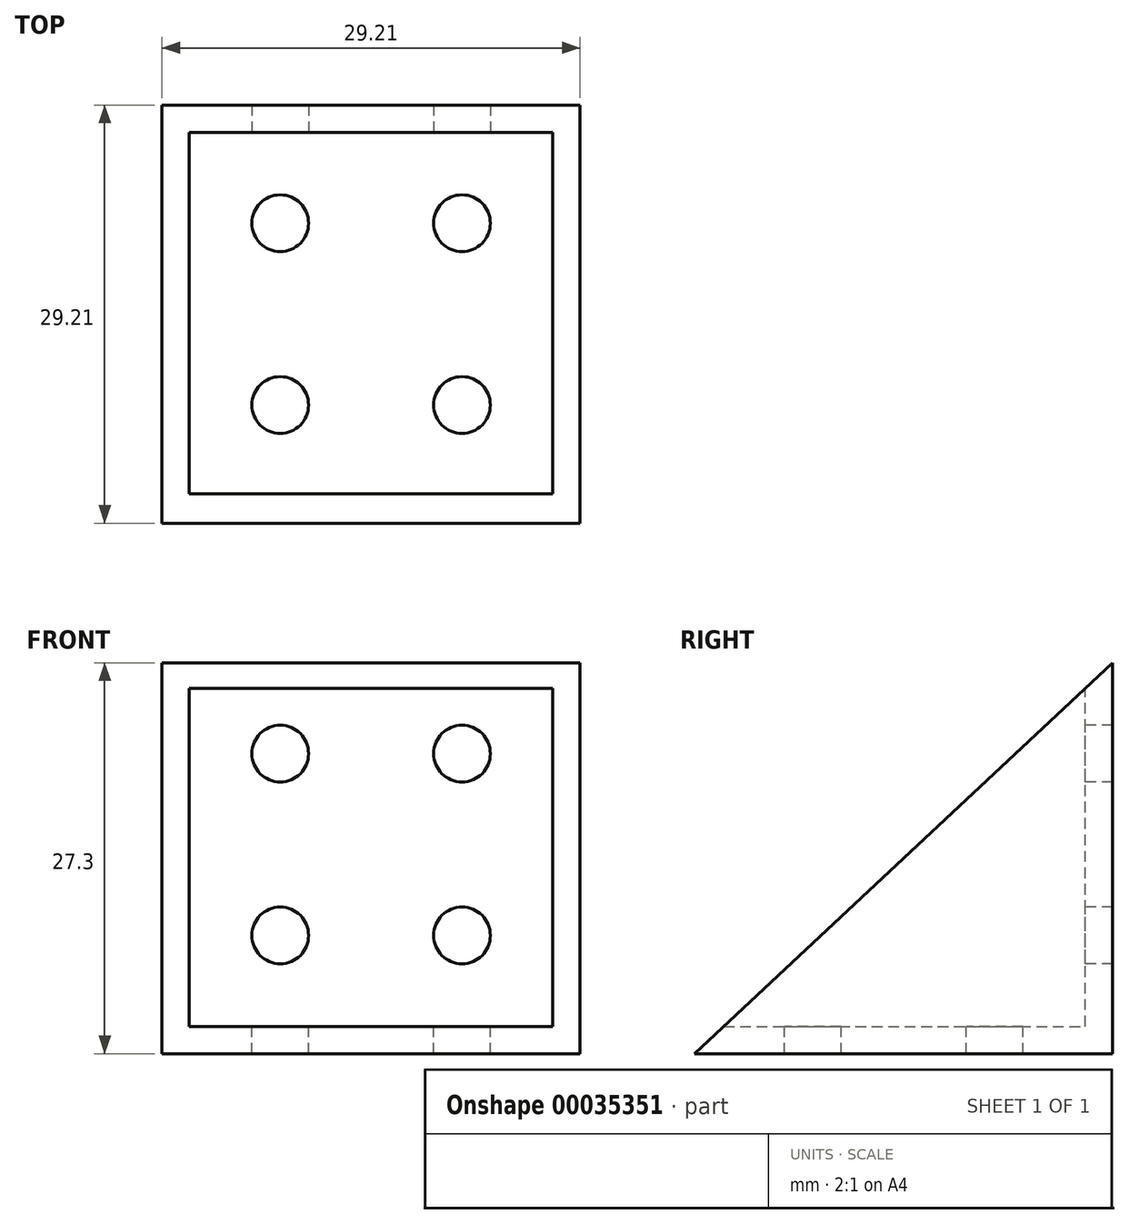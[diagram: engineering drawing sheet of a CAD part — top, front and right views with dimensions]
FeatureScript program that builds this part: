
annotation { "Feature Type Name" : "Feature", "Feature Type Description" : "" }
export const myFeature = defineFeature(function(context is Context, id is Id, definition is map)
    precondition{}
    {
        {
            var Q0;
            Q0=qCreatedBy(makeId("Top.planeOp"),FACE);
            var sketch = newSketch(context, id + "F0", { "sketchPlane" : qUnion([Q0])});
            skLineSegment(sketch, "E0.bottom", {"start": v(-238.8, 36.6) * mm, "end": v(-209.59, 36.6) * mm});
            skLineSegment(sketch, "E0.top", {"start": v(-238.8, 7.4) * mm, "end": v(-209.59, 7.4) * mm});
            skLineSegment(sketch, "E0.left", {"start": v(-238.8, 36.6) * mm, "end": v(-238.8, 7.4) * mm});
            skLineSegment(sketch, "E0.right", {"start": v(-209.59, 36.6) * mm, "end": v(-209.59, 7.4) * mm});
            skSolve(sketch);
        }
        {
            var Q0;
            Q0=makeQuery(id+"F0.imprint","IMPRINT",FACE,{"disambiguationData":[TD([[makeQuery(id+"F0.imprint","IMPRINT",EDGE,{"derivedFrom":sQuery(id+"F0.wireOp",EDGE,"E0.bottom")}),-1.0]])]});
            extrude(context, id + "F1", {"entities" : qUnion([Q0]), "depth" : 27.3 * mm});
        }
        {
            var Q0;
            Q0=makeQuery(id+"F1.opExtrude","CAP_FACE",FACE,{"disambiguationData":[OSD([sQuery(id+"F0.wireOp",EDGE,"E0.bottom"),sQuery(id+"F0.wireOp",EDGE,"E0.top"),sQuery(id+"F0.wireOp",EDGE,"E0.left"),sQuery(id+"F0.wireOp",EDGE,"E0.right")])],"isStart":false});
            var sketch = newSketch(context, id + "F2", { "sketchPlane" : qUnion([Q0])});
            skLineSegment(sketch, "E1", {"start": v(-236.9, 7.4) * mm, "end": v(-236.9, 34.7) * mm});
            skLineSegment(sketch, "E2", {"start": v(-236.9, 34.7) * mm, "end": v(-224.2, 34.7) * mm});
            skLineSegment(sketch, "E3.MirrorCS", {"start": v(-211.5, 34.7) * mm, "end": v(-224.2, 34.7) * mm});
            skLineSegment(sketch, "E4.MirrorCS", {"start": v(-211.5, 7.4) * mm, "end": v(-211.5, 34.7) * mm});
            skSolve(sketch);
        }
        {
            var Q0;
            Q0=makeQuery(id+"F1.opExtrude","SWEPT_FACE",FACE,{"disambiguationData":[OSD([sQuery(id+"F0.wireOp",EDGE,"E0.left")])]});
            var sketch = newSketch(context, id + "F3", { "sketchPlane" : qUnion([Q0])});
            skLineSegment(sketch, "E5", {"start": v(-36.6, 27.3) * mm, "end": v(-7.4, 0) * mm});
            skSolve(sketch);
        }
        {
            var Q0;
            {var subQ2=sQuery(id+"F2.wireOp",EDGE,"E1");Q0=makeQuery(id+"F2.imprint","IMPRINT",FACE,{"disambiguationData":[TD([[makeQuery(id+"F2.imprint","IMPRINT",EDGE,{"derivedFrom":subQ2}),-1.0]])]});}
            extrude(context, id + "F4", {"entities" : qUnion([Q0]), "operationType" : NewBodyOperationType.REMOVE, "oppositeDirection" : true, "depth" : 25.4 * mm});
        }
        {
            var Q0;
            Q0=makeQuery(id+"F3.imprint","IMPRINT",FACE,{"disambiguationData":[TD([[makeQuery(id+"F3.imprint","IMPRINT",EDGE,{"derivedFrom":sQuery(id+"F3.wireOp",EDGE,"E5")}),1.0]])]});
            extrude(context, id + "F5", {"entities" : qUnion([Q0]), "operationType" : NewBodyOperationType.REMOVE, "oppositeDirection" : true, "depth" : 29.2 * mm});
        }
        {
            var Q0;
            Q0=makeQuery(id+"F4.boolean.opBoolean","COPY",FACE,{"derivedFrom":makeQuery(id+"F4.opExtrude","CAP_FACE",FACE,{"disambiguationData":[OSD([sQuery(id+"F0.wireOp",EDGE,"E0.top"),sQuery(id+"F2.wireOp",EDGE,"E1"),sQuery(id+"F2.wireOp",EDGE,"E2"),sQuery(id+"F2.wireOp",EDGE,"E3.MirrorCS"),sQuery(id+"F2.wireOp",EDGE,"E4.MirrorCS")])],"isStart":false})});
            var sketch = newSketch(context, id + "F6", { "sketchPlane" : qUnion([Q0])});
            skCircle(sketch, "E6", {"center": v(-230.54, 28.35) * mm, "radius": 1.98 * mm});
            skCircle(sketch, "E7", {"center": v(-217.84, 28.35) * mm, "radius": 1.98 * mm});
            skCircle(sketch, "E8", {"center": v(-230.54, 15.65) * mm, "radius": 1.98 * mm});
            skCircle(sketch, "E9", {"center": v(-217.84, 15.65) * mm, "radius": 1.98 * mm});
            skSolve(sketch);
        }
        {
            var Q0;
            Q0=makeQuery(id+"F4.boolean.opBoolean","COPY",FACE,{"derivedFrom":makeQuery(id+"F4.opExtrude","SWEPT_FACE",FACE,{"disambiguationData":[OSD([sQuery(id+"F2.wireOp",EDGE,"E2"),sQuery(id+"F2.wireOp",EDGE,"E3.MirrorCS")])]})});
            var sketch = newSketch(context, id + "F7", { "sketchPlane" : qUnion([Q0])});
            skCircle(sketch, "E10", {"center": v(-230.54, 20.96) * mm, "radius": 1.98 * mm});
            skCircle(sketch, "E11", {"center": v(-217.84, 20.96) * mm, "radius": 1.98 * mm});
            skCircle(sketch, "E12", {"center": v(-217.84, 8.26) * mm, "radius": 1.98 * mm});
            skCircle(sketch, "E13", {"center": v(-230.54, 8.26) * mm, "radius": 1.98 * mm});
            skSolve(sketch);
        }
        {
            var Q0;
            Q0=makeQuery(id+"F6.imprint","IMPRINT",FACE,{"disambiguationData":[TD([[makeQuery(id+"F6.imprint","IMPRINT",EDGE,{"derivedFrom":sQuery(id+"F6.wireOp",EDGE,"E6")}),1.0]])]});
            var Q1;
            Q1=makeQuery(id+"F6.imprint","IMPRINT",FACE,{"disambiguationData":[TD([[makeQuery(id+"F6.imprint","IMPRINT",EDGE,{"derivedFrom":sQuery(id+"F6.wireOp",EDGE,"E7")}),1.0]])]});
            var Q2;
            Q2=makeQuery(id+"F6.imprint","IMPRINT",FACE,{"disambiguationData":[TD([[makeQuery(id+"F6.imprint","IMPRINT",EDGE,{"derivedFrom":sQuery(id+"F6.wireOp",EDGE,"E9")}),1.0]])]});
            var Q3;
            Q3=makeQuery(id+"F6.imprint","IMPRINT",FACE,{"disambiguationData":[TD([[makeQuery(id+"F6.imprint","IMPRINT",EDGE,{"derivedFrom":sQuery(id+"F6.wireOp",EDGE,"E8")}),1.0]])]});
            extrude(context, id + "F8", {"entities" : qUnion([Q0, Q1, Q2, Q3]), "operationType" : NewBodyOperationType.REMOVE, "oppositeDirection" : true, "depth" : 25.4 * mm});
        }
        {
            var Q0;
            Q0=makeQuery(id+"F7.imprint","IMPRINT",FACE,{"disambiguationData":[TD([[makeQuery(id+"F7.imprint","IMPRINT",EDGE,{"derivedFrom":sQuery(id+"F7.wireOp",EDGE,"E13")}),1.0]])]});
            var Q1;
            Q1=makeQuery(id+"F7.imprint","IMPRINT",FACE,{"disambiguationData":[TD([[makeQuery(id+"F7.imprint","IMPRINT",EDGE,{"derivedFrom":sQuery(id+"F7.wireOp",EDGE,"E10")}),1.0]])]});
            var Q2;
            Q2=makeQuery(id+"F7.imprint","IMPRINT",FACE,{"disambiguationData":[TD([[makeQuery(id+"F7.imprint","IMPRINT",EDGE,{"derivedFrom":sQuery(id+"F7.wireOp",EDGE,"E11")}),1.0]])]});
            var Q3;
            Q3=makeQuery(id+"F7.imprint","IMPRINT",FACE,{"disambiguationData":[TD([[makeQuery(id+"F7.imprint","IMPRINT",EDGE,{"derivedFrom":sQuery(id+"F7.wireOp",EDGE,"E12")}),1.0]])]});
            extrude(context, id + "F9", {"entities" : qUnion([Q0, Q1, Q2, Q3]), "operationType" : NewBodyOperationType.REMOVE, "oppositeDirection" : true, "depth" : 25.4 * mm});
        }
    });
